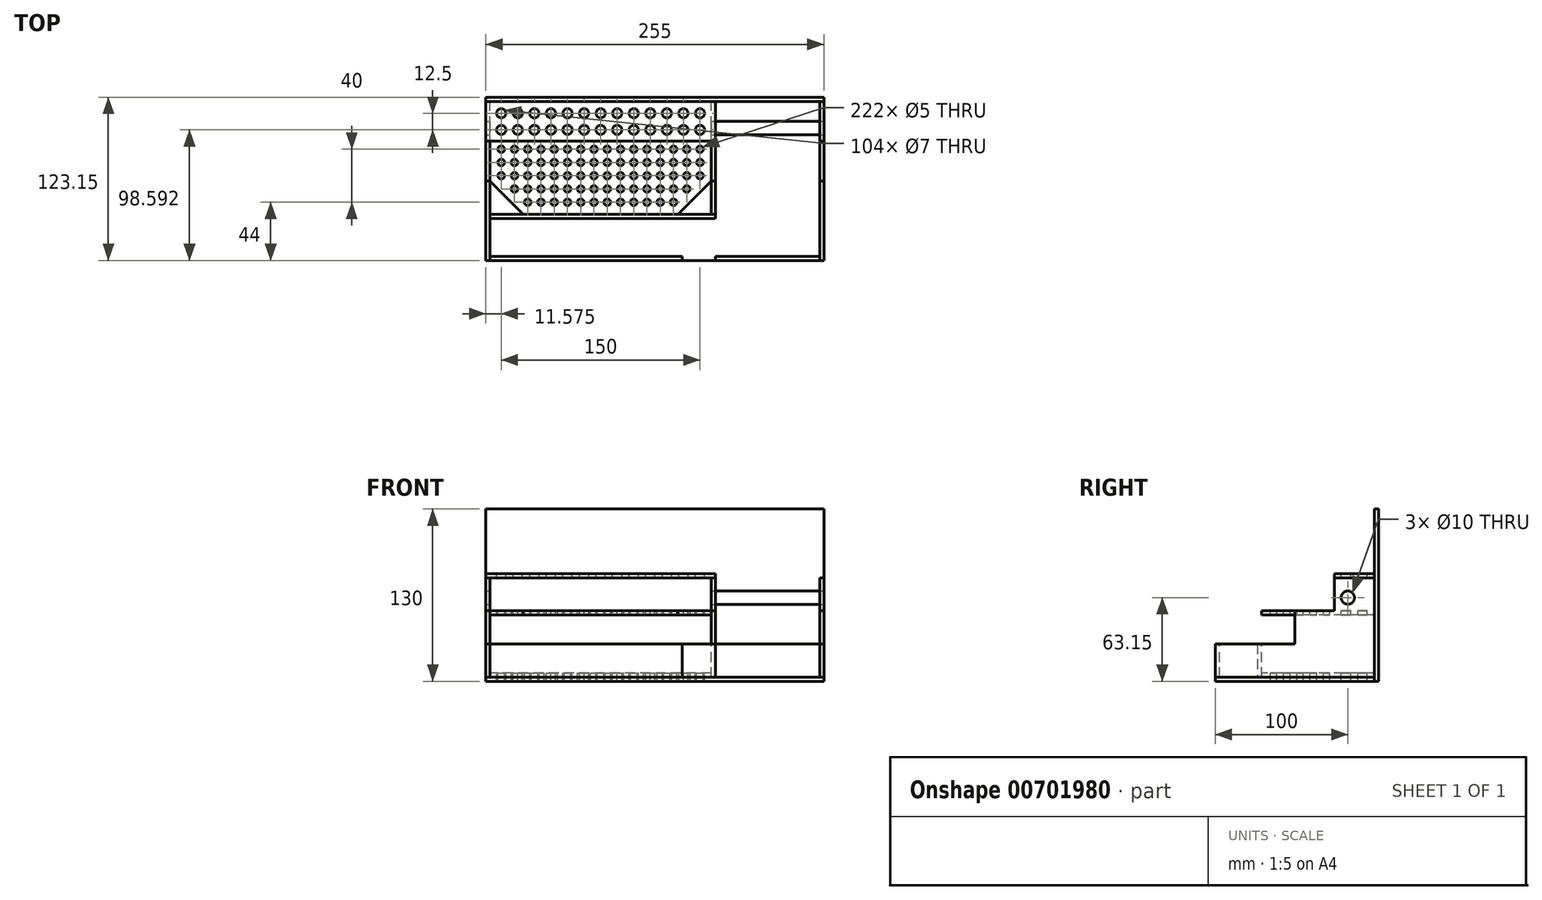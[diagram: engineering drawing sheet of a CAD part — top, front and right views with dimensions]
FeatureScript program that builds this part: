
annotation { "Feature Type Name" : "Feature", "Feature Type Description" : "" }
export const myFeature = defineFeature(function(context is Context, id is Id, definition is map)
    precondition{}
    {
        {
            assignVariable(context, id + "F0", {"name" : "x", "anyValue" : 3.15});
        }
        {
            var Q0;
            Q0=qCreatedBy(makeId("Top.planeOp"),FACE);
            var sketch = newSketch(context, id + "F1", { "sketchPlane" : qUnion([Q0])});
            skLineSegment(sketch, "E0.bottom", {"start": v(0, 0) * mm, "end": v(255, 0) * mm});
            skLineSegment(sketch, "E0.top", {"start": v(0, 120) * mm, "end": v(255, 120) * mm});
            skLineSegment(sketch, "E0.left", {"start": v(0, 0) * mm, "end": v(0, 120) * mm});
            skLineSegment(sketch, "E0.right", {"start": v(255, 0) * mm, "end": v(255, 120) * mm});
            skSolve(sketch);
        }
        {
            var Q0;
            Q0=qSketchRegion(id+"F1",true);
            extrude(context, id + "F2", {"entities" : qUnion([Q0]), "depth" : (getVariable(context, 'x')) * mm, "offsetDistance" : 25 * mm});
        }
        {
            var Q0;
            Q0=makeQuery(id+"F2.opExtrude","SWEPT_FACE",FACE,{"disambiguationData":[OSD([sQuery(id+"F1.wireOp",EDGE,"E0.left")])]});
            var sketch = newSketch(context, id + "F3", { "sketchPlane" : qUnion([Q0])});
            skLineSegment(sketch, "E1.left", {"start": v(0, 3.15) * mm, "end": v(0, 28.15) * mm});
            skLineSegment(sketch, "E2", {"start": v(0, 3.15) * mm, "end": v(-120, 3.15) * mm});
            skLineSegment(sketch, "E3", {"start": v(-120, 3.15) * mm, "end": v(-120, 78.15) * mm});
            skLineSegment(sketch, "E4", {"start": v(0, 28.15) * mm, "end": v(-60, 28.15) * mm});
            skLineSegment(sketch, "E5", {"start": v(-60, 28.15) * mm, "end": v(-60, 53.15) * mm});
            skLineSegment(sketch, "E6", {"start": v(-60, 53.15) * mm, "end": v(-90, 53.15) * mm});
            skLineSegment(sketch, "E7", {"start": v(-90, 53.15) * mm, "end": v(-90, 78.15) * mm});
            skLineSegment(sketch, "E8", {"start": v(-90, 78.15) * mm, "end": v(-120, 78.15) * mm});
            skLineSegment(sketch, "E9", {"start": v(-90, 53.15) * mm, "end": v(-90, 3.15) * mm, "construction": true});
            skLineSegment(sketch, "E10", {"start": v(-60, 28.15) * mm, "end": v(-90, 28.15) * mm, "construction": true});
            skSolve(sketch);
        }
        {
            var Q0;
            Q0=qSketchRegion(id+"F3",true);
            extrude(context, id + "F4", {"entities" : qUnion([Q0]), "oppositeDirection" : true, "depth" : (getVariable(context, 'x')) * mm, "offsetDistance" : 25 * mm});
        }
        {
            var Q0;
            Q0=makeQuery(id+"F4.opExtrude","SWEPT_BODY",BODY,{"disambiguationData":[OSD([sQuery(id+"F3.wireOp",EDGE,"E1.top"),sQuery(id+"F3.wireOp",EDGE,"E1.left"),sQuery(id+"F3.wireOp",EDGE,"E2"),sQuery(id+"F3.wireOp",EDGE,"E3")])]});
            transform(context, id + "F5", {"entities" : qUnion([Q0]), "transformType" : TransformType.TRANSLATION_3D, "dx" : (263.7 + 3.15 - 15) * mm, "dy" : 0 * mm, "dz" : 0 * mm, "makeCopy" : true});
        }
        {
            var Q0;
            Q0=makeQuery(id+"F4.opExtrude","SWEPT_BODY",BODY,{"disambiguationData":[OSD([sQuery(id+"F3.wireOp",EDGE,"E1.left"),sQuery(id+"F3.wireOp",EDGE,"E2"),sQuery(id+"F3.wireOp",EDGE,"E3"),sQuery(id+"F3.wireOp",EDGE,"E4"),sQuery(id+"F3.wireOp",EDGE,"E5"),sQuery(id+"F3.wireOp",EDGE,"E6"),sQuery(id+"F3.wireOp",EDGE,"E7"),sQuery(id+"F3.wireOp",EDGE,"E8")])]});
            transform(context, id + "F6", {"entities" : qUnion([Q0]), "transformType" : TransformType.TRANSLATION_3D, "dx" : 170 * mm, "dy" : 0 * mm, "dz" : 0 * mm, "makeCopy" : true});
        }
        {
            var Q0;
            Q0=makeQuery(id+"F4.opExtrude","SWEPT_FACE",FACE,{"disambiguationData":[OSD([sQuery(id+"F3.wireOp",EDGE,"E5")])]});
            var sketch = newSketch(context, id + "F7", { "sketchPlane" : qUnion([Q0])});
            skLineSegment(sketch, "E11.bottom", {"start": v(3.15, 6.3) * mm, "end": v(170, 6.3) * mm});
            skLineSegment(sketch, "E11.top", {"start": v(3.15, 3.15) * mm, "end": v(170, 3.15) * mm});
            skLineSegment(sketch, "E11.right", {"start": v(170, 6.3) * mm, "end": v(170, 3.15) * mm});
            skLineSegment(sketch, "E12", {"start": v(3.15, 3.15) * mm, "end": v(3.15, 6.3) * mm});
            skSolve(sketch);
        }
        {
            var Q0;
            Q0=qSketchRegion(id+"F7",true);
            var Q1;
            Q1=makeQuery(id+"F4.opExtrude","SWEPT_FACE",FACE,{"disambiguationData":[OSD([sQuery(id+"F3.wireOp",EDGE,"E3")])]});
            extrude(context, id + "F8", {"entities" : qUnion([Q0]), "endBound" : BoundingType.UP_TO_SURFACE, "oppositeDirection" : true, "depth" : 25 * mm, "endBoundEntityFace" : qUnion([Q1]), "offsetDistance" : 25 * mm, "hasSecondDirection" : true, "secondDirectionOppositeDirection" : false, "secondDirectionDepth" : 25 * mm});
        }
        {
            var Q0;
            Q0=makeQuery(id+"F4.opExtrude","SWEPT_FACE",FACE,{"disambiguationData":[OSD([sQuery(id+"F3.wireOp",EDGE,"E5")])]});
            var sketch = newSketch(context, id + "F9", { "sketchPlane" : qUnion([Q0])});
            skLineSegment(sketch, "E13.bottom", {"start": v(3.15, 53.15) * mm, "end": v(170, 53.15) * mm});
            skLineSegment(sketch, "E13.top", {"start": v(3.15, 50) * mm, "end": v(170, 50) * mm});
            skLineSegment(sketch, "E13.left", {"start": v(3.15, 50) * mm, "end": v(3.15, 53.15) * mm});
            skLineSegment(sketch, "E13.right", {"start": v(170, 53.15) * mm, "end": v(170, 50) * mm});
            skSolve(sketch);
        }
        {
            var Q0;
            Q0=qSketchRegion(id+"F9",true);
            var Q1;
            Q1=makeQuery(id+"F4.opExtrude","SWEPT_FACE",FACE,{"disambiguationData":[OSD([sQuery(id+"F3.wireOp",EDGE,"E3")])]});
            extrude(context, id + "F10", {"entities" : qUnion([Q0]), "endBound" : BoundingType.UP_TO_SURFACE, "oppositeDirection" : true, "depth" : 25 * mm, "endBoundEntityFace" : qUnion([Q1]), "offsetDistance" : 25 * mm, "hasSecondDirection" : true, "secondDirectionOppositeDirection" : false, "secondDirectionDepth" : 25 * mm});
        }
        {
            var Q0;
            Q0=makeQuery(id+"F2.opExtrude","SWEPT_FACE",FACE,{"disambiguationData":[OSD([sQuery(id+"F1.wireOp",EDGE,"E0.top")])]});
            var sketch = newSketch(context, id + "F11", { "sketchPlane" : qUnion([Q0])});
            skLineSegment(sketch, "E14.bottom", {"start": v(-255, 130) * mm, "end": v(0, 130) * mm});
            skLineSegment(sketch, "E14.top", {"start": v(-255, 0) * mm, "end": v(0, 0) * mm});
            skLineSegment(sketch, "E14.left", {"start": v(-255, 130) * mm, "end": v(-255, 0) * mm});
            skLineSegment(sketch, "E14.right", {"start": v(0, 130) * mm, "end": v(0, 0) * mm});
            skSolve(sketch);
        }
        {
            var Q0;
            Q0=qSketchRegion(id+"F11",true);
            extrude(context, id + "F12", {"entities" : qUnion([Q0]), "depth" : (getVariable(context, 'x')) * mm, "offsetDistance" : 25 * mm});
        }
        {
            var Q0;
            Q0=makeQuery(id+"F4.opExtrude","SWEPT_FACE",FACE,{"disambiguationData":[OSD([sQuery(id+"F3.wireOp",EDGE,"E1.left")])]});
            var sketch = newSketch(context, id + "F13", { "sketchPlane" : qUnion([Q0])});
            skLineSegment(sketch, "E15.bottom", {"start": v(3.15, 3.15) * mm, "end": v(251.85, 3.15) * mm});
            skLineSegment(sketch, "E15.top", {"start": v(3.15, 28.15) * mm, "end": v(251.85, 28.15) * mm});
            skLineSegment(sketch, "E15.left", {"start": v(3.15, 3.15) * mm, "end": v(3.15, 28.15) * mm});
            skLineSegment(sketch, "E15.right", {"start": v(251.85, 3.15) * mm, "end": v(251.85, 28.15) * mm});
            skSolve(sketch);
        }
        {
            var Q0;
            Q0 = qSketchRegion(id + "F13", true);
            extrude(context, id + "F14", {"entities" : qUnion([Q0]), "oppositeDirection" : true, "depth" : (getVariable(context, 'x')) * mm, "offsetDistance" : 25 * mm});
        }
        {
            var Q0;
            Q0=makeQuery(id+"F6.opPattern","COPY",FACE,{"derivedFrom":makeQuery(id+"F4.opExtrude","CAP_FACE",FACE,{"disambiguationData":[OSD([sQuery(id+"F3.wireOp",EDGE,"E1.left"),sQuery(id+"F3.wireOp",EDGE,"E2"),sQuery(id+"F3.wireOp",EDGE,"E3"),sQuery(id+"F3.wireOp",EDGE,"E4"),sQuery(id+"F3.wireOp",EDGE,"E5"),sQuery(id+"F3.wireOp",EDGE,"E6"),sQuery(id+"F3.wireOp",EDGE,"E7"),sQuery(id+"F3.wireOp",EDGE,"E8")])],"isStart":false}),"instanceName":"1"});
            var sketch = newSketch(context, id + "F15", { "sketchPlane" : qUnion([Q0])});
            skLineSegment(sketch, "E16.bottom", {"start": v(0, 28.15) * mm, "end": v(35, 28.15) * mm});
            skLineSegment(sketch, "E16.top", {"start": v(0, 3.15) * mm, "end": v(35, 3.15) * mm});
            skLineSegment(sketch, "E16.left", {"start": v(0, 28.15) * mm, "end": v(0, 3.15) * mm});
            skLineSegment(sketch, "E16.right", {"start": v(35, 28.15) * mm, "end": v(35, 3.15) * mm});
            skSolve(sketch);
        }
        {
            var Q0;
            Q0 = qSketchRegion(id + "F15", true);
            extrude(context, id + "F16", {"entities" : qUnion([Q0]), "operationType" : NewBodyOperationType.REMOVE, "oppositeDirection" : true, "depth" : 25 * mm, "offsetDistance" : 25 * mm});
        }
        {
            var Q0;
            Q0=makeQuery(id+"F16.boolean.opBoolean","COPY",FACE,{"derivedFrom":makeQuery(id+"F16.opExtrude","SWEPT_FACE",FACE,{"disambiguationData":[OSD([sQuery(id+"F15.wireOp",EDGE,"E16.right")])]})});
            var sketch = newSketch(context, id + "F17", { "sketchPlane" : qUnion([Q0])});
            skLineSegment(sketch, "E17.bottom", {"start": v(173.15, 28.15) * mm, "end": v(3.15, 28.15) * mm});
            skLineSegment(sketch, "E17.top", {"start": v(173.15, 3.15) * mm, "end": v(3.15, 3.15) * mm});
            skLineSegment(sketch, "E17.left", {"start": v(173.15, 28.15) * mm, "end": v(173.15, 3.15) * mm});
            skLineSegment(sketch, "E17.right", {"start": v(3.15, 28.15) * mm, "end": v(3.15, 3.15) * mm});
            skSolve(sketch);
        }
        {
            var Q0;
            Q0 = qSketchRegion(id + "F17", true);
            extrude(context, id + "F18", {"entities" : qUnion([Q0]), "depth" : (getVariable(context, 'x')) * mm, "offsetDistance" : 25 * mm});
        }
        {
            var Q0;
            Q0=makeQuery(id+"F10.opExtrude","SWEPT_FACE",FACE,{"disambiguationData":[OSD([sQuery(id+"F9.wireOp",EDGE,"E13.bottom")])]});
            var sketch = newSketch(context, id + "F19", { "sketchPlane" : qUnion([Q0])});
            skLineSegment(sketch, "E18", {"start": v(3.15, 60) * mm, "end": v(28.15, 35) * mm});
            skLineSegment(sketch, "E19", {"start": v(28.15, 35) * mm, "end": v(3.15, 35) * mm});
            skLineSegment(sketch, "E20", {"start": v(3.15, 35) * mm, "end": v(3.15, 60) * mm});
            skLineSegment(sketch, "E21", {"start": v(170, 60) * mm, "end": v(145, 35) * mm});
            skLineSegment(sketch, "E22", {"start": v(145, 35) * mm, "end": v(170, 35) * mm});
            skLineSegment(sketch, "E23", {"start": v(170, 35) * mm, "end": v(170, 60) * mm});
            skSolve(sketch);
        }
        {
            var Q0;
            Q0 = qSketchRegion(id + "F19", true);
            extrude(context, id + "F20", {"entities" : qUnion([Q0]), "operationType" : NewBodyOperationType.REMOVE, "oppositeDirection" : true, "depth" : 25 * mm, "offsetDistance" : 25 * mm});
        }
        {
            var Q0;
            Q0=makeQuery(id+"F4.opExtrude","SWEPT_FACE",FACE,{"disambiguationData":[OSD([sQuery(id+"F3.wireOp",EDGE,"E8")])]});
            var sketch = newSketch(context, id + "F21", { "sketchPlane" : qUnion([Q0])});
            skLineSegment(sketch, "E24.bottom", {"start": v(0, 90) * mm, "end": v(173.15, 90) * mm});
            skLineSegment(sketch, "E24.top", {"start": v(0, 120) * mm, "end": v(173.15, 120) * mm});
            skLineSegment(sketch, "E24.left", {"start": v(0, 90) * mm, "end": v(0, 120) * mm});
            skLineSegment(sketch, "E24.right", {"start": v(173.15, 90) * mm, "end": v(173.15, 120) * mm});
            skSolve(sketch);
        }
        {
            var Q0;
            Q0 = qSketchRegion(id + "F21", true);
            extrude(context, id + "F22", {"entities" : qUnion([Q0]), "depth" : (getVariable(context, 'x')) * mm, "offsetDistance" : 25 * mm});
        }
        {
            var Q0;
            Q0=makeQuery(id+"F22.opExtrude","CAP_FACE",FACE,{"disambiguationData":[OSD([sQuery(id+"F21.wireOp",EDGE,"E24.bottom"),sQuery(id+"F21.wireOp",EDGE,"E24.top"),sQuery(id+"F21.wireOp",EDGE,"E24.left"),sQuery(id+"F21.wireOp",EDGE,"E24.right")])],"isStart":false});
            var sketch = newSketch(context, id + "F23", { "sketchPlane" : qUnion([Q0])});
            skCircle(sketch, "E25", {"center": v(11.58, 111.1) * mm, "radius": 3.5 * mm});
            skCircle(sketch, "E26.0.1.0", {"center": v(11.58, 98.6) * mm, "radius": 3.5 * mm});
            skCircle(sketch, "E26.1.0.0", {"center": v(24.08, 111.1) * mm, "radius": 3.5 * mm});
            skCircle(sketch, "E26.1.1.0", {"center": v(24.08, 98.6) * mm, "radius": 3.5 * mm});
            skCircle(sketch, "E26.2.0.0", {"center": v(36.58, 111.1) * mm, "radius": 3.5 * mm});
            skCircle(sketch, "E26.2.1.0", {"center": v(36.58, 98.6) * mm, "radius": 3.5 * mm});
            skCircle(sketch, "E26.3.0.0", {"center": v(49.08, 111.1) * mm, "radius": 3.5 * mm});
            skCircle(sketch, "E26.3.1.0", {"center": v(49.08, 98.6) * mm, "radius": 3.5 * mm});
            skCircle(sketch, "E26.4.0.0", {"center": v(61.58, 111.1) * mm, "radius": 3.5 * mm});
            skCircle(sketch, "E26.4.1.0", {"center": v(61.58, 98.6) * mm, "radius": 3.5 * mm});
            skCircle(sketch, "E26.5.0.0", {"center": v(74.08, 111.1) * mm, "radius": 3.5 * mm});
            skCircle(sketch, "E26.5.1.0", {"center": v(74.08, 98.6) * mm, "radius": 3.5 * mm});
            skCircle(sketch, "E26.6.0.0", {"center": v(86.58, 111.1) * mm, "radius": 3.5 * mm});
            skCircle(sketch, "E26.6.1.0", {"center": v(86.58, 98.6) * mm, "radius": 3.5 * mm});
            skCircle(sketch, "E26.7.0.0", {"center": v(99.08, 111.1) * mm, "radius": 3.5 * mm});
            skCircle(sketch, "E26.7.1.0", {"center": v(99.08, 98.6) * mm, "radius": 3.5 * mm});
            skCircle(sketch, "E26.8.0.0", {"center": v(111.58, 111.1) * mm, "radius": 3.5 * mm});
            skCircle(sketch, "E26.8.1.0", {"center": v(111.58, 98.6) * mm, "radius": 3.5 * mm});
            skCircle(sketch, "E26.9.0.0", {"center": v(124.08, 111.1) * mm, "radius": 3.5 * mm});
            skCircle(sketch, "E26.9.1.0", {"center": v(124.08, 98.6) * mm, "radius": 3.5 * mm});
            skCircle(sketch, "E26.10.0.0", {"center": v(136.57, 111.1) * mm, "radius": 3.5 * mm});
            skCircle(sketch, "E26.10.1.0", {"center": v(136.57, 98.6) * mm, "radius": 3.5 * mm});
            skCircle(sketch, "E26.11.0.0", {"center": v(149.08, 111.1) * mm, "radius": 3.5 * mm});
            skCircle(sketch, "E26.11.1.0", {"center": v(149.08, 98.6) * mm, "radius": 3.5 * mm});
            skCircle(sketch, "E26.12.0.0", {"center": v(161.58, 111.1) * mm, "radius": 3.5 * mm});
            skCircle(sketch, "E26.12.1.0", {"center": v(161.58, 98.6) * mm, "radius": 3.5 * mm});
            skLineSegment(sketch, "E26.direction1", {"start": v(11.58, 111.1) * mm, "end": v(24.08, 111.1) * mm, "construction": true});
            skLineSegment(sketch, "E26.direction2", {"start": v(11.58, 111.1) * mm, "end": v(11.58, 98.6) * mm, "construction": true});
            skLineSegment(sketch, "E27", {"start": v(86.58, 90) * mm, "end": v(86.58, 98.6) * mm, "construction": true});
            skLineSegment(sketch, "E28", {"start": v(0, 105) * mm, "end": v(11.58, 105) * mm, "construction": true});
            skPoint(sketch, "E28.endSnap0", {"position": v(11.58, 104.84) * mm});
            skCircle(sketch, "E29", {"center": v(11.58, 84) * mm, "radius": 2.5 * mm});
            skCircle(sketch, "E30.0.1.0", {"center": v(11.58, 74) * mm, "radius": 2.5 * mm});
            skCircle(sketch, "E30.0.2.0", {"center": v(11.58, 64) * mm, "radius": 2.5 * mm});
            skCircle(sketch, "E30.1.0.0", {"center": v(21.58, 84) * mm, "radius": 2.5 * mm});
            skCircle(sketch, "E30.1.1.0", {"center": v(21.58, 74) * mm, "radius": 2.5 * mm});
            skCircle(sketch, "E30.1.2.0", {"center": v(21.58, 64) * mm, "radius": 2.5 * mm});
            skCircle(sketch, "E30.2.0.0", {"center": v(31.58, 84) * mm, "radius": 2.5 * mm});
            skCircle(sketch, "E30.2.1.0", {"center": v(31.58, 74) * mm, "radius": 2.5 * mm});
            skCircle(sketch, "E30.2.2.0", {"center": v(31.58, 64) * mm, "radius": 2.5 * mm});
            skCircle(sketch, "E30.3.0.0", {"center": v(41.58, 84) * mm, "radius": 2.5 * mm});
            skCircle(sketch, "E30.3.1.0", {"center": v(41.58, 74) * mm, "radius": 2.5 * mm});
            skCircle(sketch, "E30.3.2.0", {"center": v(41.58, 64) * mm, "radius": 2.5 * mm});
            skCircle(sketch, "E30.4.0.0", {"center": v(51.58, 84) * mm, "radius": 2.5 * mm});
            skCircle(sketch, "E30.4.1.0", {"center": v(51.58, 74) * mm, "radius": 2.5 * mm});
            skCircle(sketch, "E30.4.2.0", {"center": v(51.58, 64) * mm, "radius": 2.5 * mm});
            skCircle(sketch, "E30.5.0.0", {"center": v(61.58, 84) * mm, "radius": 2.5 * mm});
            skCircle(sketch, "E30.5.1.0", {"center": v(61.58, 74) * mm, "radius": 2.5 * mm});
            skCircle(sketch, "E30.5.2.0", {"center": v(61.58, 64) * mm, "radius": 2.5 * mm});
            skCircle(sketch, "E30.6.0.0", {"center": v(71.58, 84) * mm, "radius": 2.5 * mm});
            skCircle(sketch, "E30.6.1.0", {"center": v(71.58, 74) * mm, "radius": 2.5 * mm});
            skCircle(sketch, "E30.6.2.0", {"center": v(71.58, 64) * mm, "radius": 2.5 * mm});
            skCircle(sketch, "E30.7.0.0", {"center": v(81.58, 84) * mm, "radius": 2.5 * mm});
            skCircle(sketch, "E30.7.1.0", {"center": v(81.58, 74) * mm, "radius": 2.5 * mm});
            skCircle(sketch, "E30.7.2.0", {"center": v(81.58, 64) * mm, "radius": 2.5 * mm});
            skCircle(sketch, "E30.8.0.0", {"center": v(91.58, 84) * mm, "radius": 2.5 * mm});
            skCircle(sketch, "E30.8.1.0", {"center": v(91.58, 74) * mm, "radius": 2.5 * mm});
            skCircle(sketch, "E30.8.2.0", {"center": v(91.58, 64) * mm, "radius": 2.5 * mm});
            skCircle(sketch, "E30.9.0.0", {"center": v(101.58, 84) * mm, "radius": 2.5 * mm});
            skCircle(sketch, "E30.9.1.0", {"center": v(101.58, 74) * mm, "radius": 2.5 * mm});
            skCircle(sketch, "E30.9.2.0", {"center": v(101.58, 64) * mm, "radius": 2.5 * mm});
            skCircle(sketch, "E30.10.0.0", {"center": v(111.58, 84) * mm, "radius": 2.5 * mm});
            skCircle(sketch, "E30.10.1.0", {"center": v(111.58, 74) * mm, "radius": 2.5 * mm});
            skCircle(sketch, "E30.10.2.0", {"center": v(111.58, 64) * mm, "radius": 2.5 * mm});
            skCircle(sketch, "E30.11.0.0", {"center": v(121.58, 84) * mm, "radius": 2.5 * mm});
            skCircle(sketch, "E30.11.1.0", {"center": v(121.58, 74) * mm, "radius": 2.5 * mm});
            skCircle(sketch, "E30.11.2.0", {"center": v(121.58, 64) * mm, "radius": 2.5 * mm});
            skCircle(sketch, "E30.12.0.0", {"center": v(131.57, 84) * mm, "radius": 2.5 * mm});
            skCircle(sketch, "E30.12.1.0", {"center": v(131.57, 74) * mm, "radius": 2.5 * mm});
            skCircle(sketch, "E30.12.2.0", {"center": v(131.57, 64) * mm, "radius": 2.5 * mm});
            skLineSegment(sketch, "E30.direction1", {"start": v(11.58, 84) * mm, "end": v(21.58, 84) * mm, "construction": true});
            skLineSegment(sketch, "E30.direction2", {"start": v(11.57, 84) * mm, "end": v(11.57, 74) * mm, "construction": true});
            skCircle(sketch, "E31.0.1.3", {"center": v(21.58, 54) * mm, "radius": 2.5 * mm});
            skCircle(sketch, "E31.0.2.3", {"center": v(31.58, 54) * mm, "radius": 2.5 * mm});
            skCircle(sketch, "E31.0.3.3", {"center": v(41.58, 54) * mm, "radius": 2.5 * mm});
            skCircle(sketch, "E31.0.4.3", {"center": v(51.58, 54) * mm, "radius": 2.5 * mm});
            skCircle(sketch, "E31.0.5.3", {"center": v(61.58, 54) * mm, "radius": 2.5 * mm});
            skCircle(sketch, "E31.0.6.3", {"center": v(71.58, 54) * mm, "radius": 2.5 * mm});
            skCircle(sketch, "E31.0.7.3", {"center": v(81.58, 54) * mm, "radius": 2.5 * mm});
            skCircle(sketch, "E31.0.8.3", {"center": v(91.58, 54) * mm, "radius": 2.5 * mm});
            skCircle(sketch, "E31.0.9.3", {"center": v(101.58, 54) * mm, "radius": 2.5 * mm});
            skCircle(sketch, "E31.0.10.3", {"center": v(111.58, 54) * mm, "radius": 2.5 * mm});
            skCircle(sketch, "E31.0.11.3", {"center": v(121.58, 54) * mm, "radius": 2.5 * mm});
            skCircle(sketch, "E31.0.12.3", {"center": v(131.57, 54) * mm, "radius": 2.5 * mm});
            skCircle(sketch, "E32.0.13.0", {"center": v(141.58, 84) * mm, "radius": 2.5 * mm});
            skCircle(sketch, "E32.0.13.1", {"center": v(141.58, 74) * mm, "radius": 2.5 * mm});
            skCircle(sketch, "E32.0.13.2", {"center": v(141.58, 64) * mm, "radius": 2.5 * mm});
            skCircle(sketch, "E32.0.13.3", {"center": v(141.58, 54) * mm, "radius": 2.5 * mm});
            skCircle(sketch, "E32.0.14.0", {"center": v(151.58, 84) * mm, "radius": 2.5 * mm});
            skCircle(sketch, "E32.0.14.1", {"center": v(151.58, 74) * mm, "radius": 2.5 * mm});
            skCircle(sketch, "E32.0.14.2", {"center": v(151.58, 64) * mm, "radius": 2.5 * mm});
            skCircle(sketch, "E32.0.14.3", {"center": v(151.58, 54) * mm, "radius": 2.5 * mm});
            skCircle(sketch, "E32.0.15.0", {"center": v(161.57, 84) * mm, "radius": 2.5 * mm});
            skCircle(sketch, "E32.0.15.1", {"center": v(161.57, 74) * mm, "radius": 2.5 * mm});
            skCircle(sketch, "E32.0.15.2", {"center": v(161.57, 64) * mm, "radius": 2.5 * mm});
            skLineSegment(sketch, "E33", {"start": v(91.58, 84) * mm, "end": v(81.58, 84) * mm, "construction": true});
            skLineSegment(sketch, "E34", {"start": v(86.58, 90) * mm, "end": v(86.58, 84) * mm, "construction": true});
            skCircle(sketch, "E35.0.2.4", {"center": v(31.58, 44) * mm, "radius": 2.5 * mm});
            skCircle(sketch, "E35.0.3.4", {"center": v(41.58, 44) * mm, "radius": 2.5 * mm});
            skCircle(sketch, "E35.0.4.4", {"center": v(51.58, 44) * mm, "radius": 2.5 * mm});
            skCircle(sketch, "E35.0.5.4", {"center": v(61.58, 44) * mm, "radius": 2.5 * mm});
            skCircle(sketch, "E35.0.6.4", {"center": v(71.58, 44) * mm, "radius": 2.5 * mm});
            skCircle(sketch, "E35.0.7.4", {"center": v(81.58, 44) * mm, "radius": 2.5 * mm});
            skCircle(sketch, "E35.0.8.4", {"center": v(91.58, 44) * mm, "radius": 2.5 * mm});
            skCircle(sketch, "E35.0.9.4", {"center": v(101.58, 44) * mm, "radius": 2.5 * mm});
            skCircle(sketch, "E35.0.10.4", {"center": v(111.58, 44) * mm, "radius": 2.5 * mm});
            skCircle(sketch, "E35.0.11.4", {"center": v(121.58, 44) * mm, "radius": 2.5 * mm});
            skCircle(sketch, "E35.0.12.4", {"center": v(131.57, 44) * mm, "radius": 2.5 * mm});
            skCircle(sketch, "E35.0.13.4", {"center": v(141.58, 44) * mm, "radius": 2.5 * mm});
            skSolve(sketch);
        }
        {
            var Q0;
            Q0 = qSketchRegion(id + "F23", true);
            extrude(context, id + "F24", {"entities" : qUnion([Q0]), "operationType" : NewBodyOperationType.REMOVE, "endBound" : BoundingType.THROUGH_ALL, "oppositeDirection" : true, "depth" : 25 * mm, "offsetDistance" : 25 * mm});
        }
        {
            var Q0;
            Q0=makeQuery(id+"F5.opPattern","COPY",FACE,{"derivedFrom":makeQuery(id+"F4.opExtrude","CAP_FACE",FACE,{"disambiguationData":[OSD([sQuery(id+"F3.wireOp",EDGE,"E1.left"),sQuery(id+"F3.wireOp",EDGE,"E2"),sQuery(id+"F3.wireOp",EDGE,"E3"),sQuery(id+"F3.wireOp",EDGE,"E4"),sQuery(id+"F3.wireOp",EDGE,"E5"),sQuery(id+"F3.wireOp",EDGE,"E6"),sQuery(id+"F3.wireOp",EDGE,"E7"),sQuery(id+"F3.wireOp",EDGE,"E8")])],"isStart":false}),"instanceName":"1"});
            var sketch = newSketch(context, id + "F25", { "sketchPlane" : qUnion([Q0])});
            skCircle(sketch, "E36", {"center": v(100, 63.15) * mm, "radius": 5 * mm});
            skLineSegment(sketch, "E37", {"start": v(100, 63.15) * mm, "end": v(100, 78.15) * mm, "construction": true});
            skSolve(sketch);
        }
        {
            var Q0;
            Q0 = qSketchRegion(id + "F25", true);
            extrude(context, id + "F26", {"entities" : qUnion([Q0]), "operationType" : NewBodyOperationType.REMOVE, "endBound" : BoundingType.THROUGH_ALL, "oppositeDirection" : true, "depth" : 25 * mm, "offsetDistance" : 25 * mm});
        }
        {
            var Q0;
            Q0=makeQuery(id+"F5.opPattern","COPY",FACE,{"derivedFrom":makeQuery(id+"F4.opExtrude","CAP_FACE",FACE,{"disambiguationData":[OSD([sQuery(id+"F3.wireOp",EDGE,"E1.left"),sQuery(id+"F3.wireOp",EDGE,"E2"),sQuery(id+"F3.wireOp",EDGE,"E3"),sQuery(id+"F3.wireOp",EDGE,"E4"),sQuery(id+"F3.wireOp",EDGE,"E5"),sQuery(id+"F3.wireOp",EDGE,"E6"),sQuery(id+"F3.wireOp",EDGE,"E7"),sQuery(id+"F3.wireOp",EDGE,"E8")])],"isStart":false}),"instanceName":"1"});
            var sketch = newSketch(context, id + "F27", { "sketchPlane" : qUnion([Q0])});
            skCircle(sketch, "E38", {"center": v(100, 63.15) * mm, "radius": 5 * mm});
            skSolve(sketch);
        }
        {
            var Q0;
            Q0 = qSketchRegion(id + "F27", true);
            var Q1;
            Q1=makeQuery(id+"F6.opPattern","COPY",FACE,{"derivedFrom":makeQuery(id+"F4.opExtrude","CAP_FACE",FACE,{"disambiguationData":[OSD([sQuery(id+"F3.wireOp",EDGE,"E1.left"),sQuery(id+"F3.wireOp",EDGE,"E2"),sQuery(id+"F3.wireOp",EDGE,"E3"),sQuery(id+"F3.wireOp",EDGE,"E4"),sQuery(id+"F3.wireOp",EDGE,"E5"),sQuery(id+"F3.wireOp",EDGE,"E6"),sQuery(id+"F3.wireOp",EDGE,"E7"),sQuery(id+"F3.wireOp",EDGE,"E8")])],"isStart":true}),"instanceName":"1"});
            extrude(context, id + "F28", {"entities" : qUnion([Q0]), "endBound" : BoundingType.UP_TO_SURFACE, "oppositeDirection" : true, "depth" : 25 * mm, "endBoundEntityFace" : qUnion([Q1]), "offsetDistance" : 25 * mm});
        }
    });
